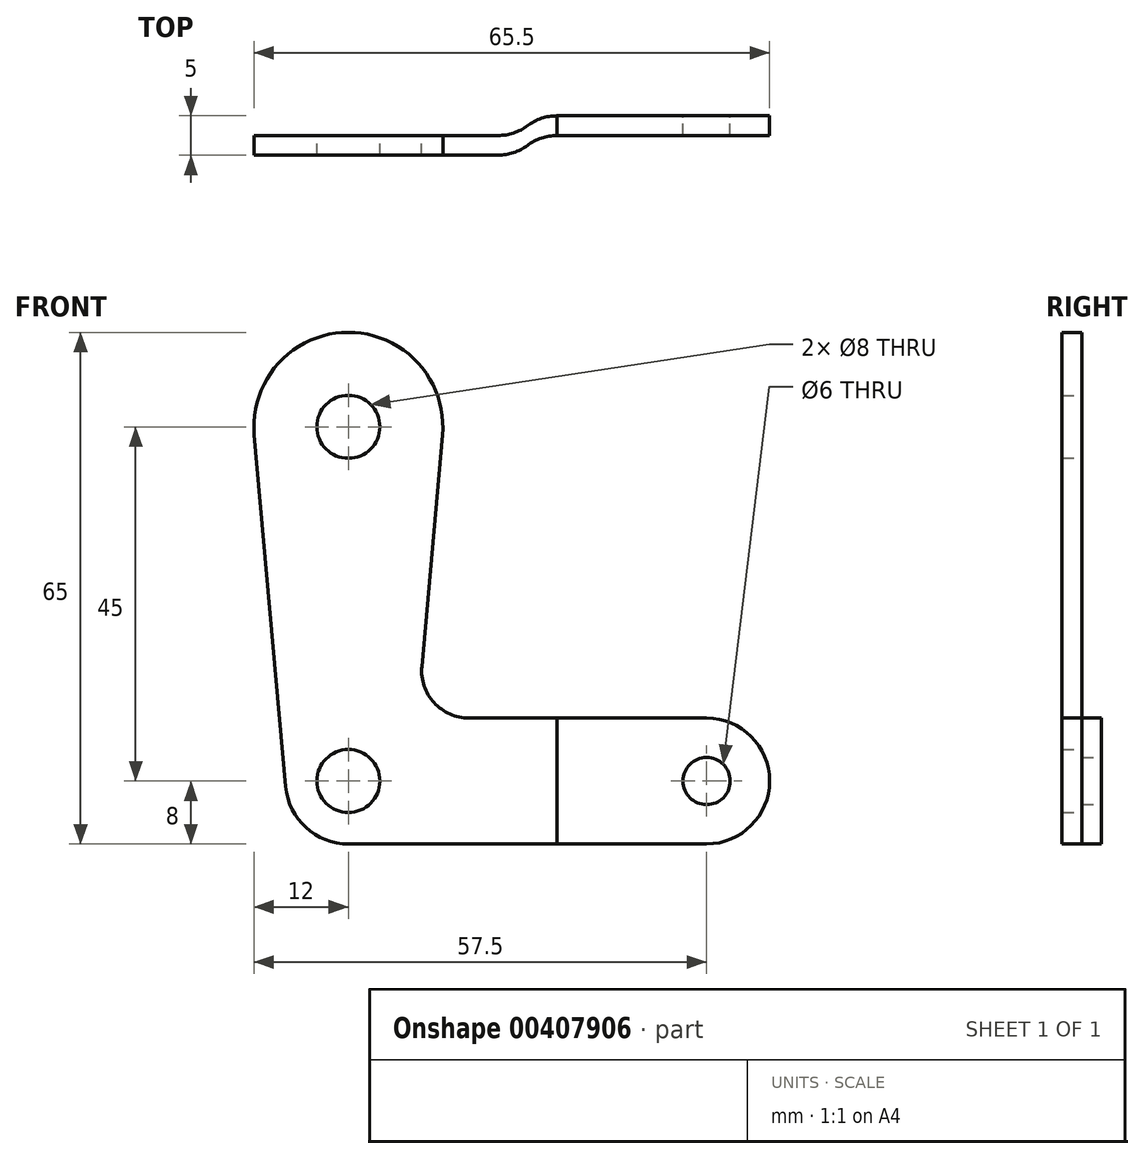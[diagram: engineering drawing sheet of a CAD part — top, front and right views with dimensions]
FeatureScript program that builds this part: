
annotation { "Feature Type Name" : "Feature", "Feature Type Description" : "" }
export const myFeature = defineFeature(function(context is Context, id is Id, definition is map)
    precondition{}
    {
        {
            var Q0;
            Q0=qCreatedBy(makeId("Front.planeOp"),FACE);
            var sketch = newSketch(context, id + "F0", { "sketchPlane" : qUnion([Q0])});
            skCircle(sketch, "E0", {"center": v(0, 0) * mm, "radius": 4 * mm});
            skCircle(sketch, "E1", {"center": v(0, 45) * mm, "radius": 4 * mm});
            skArc(sketch, "E2", {"start": v(0, -8) * mm, "mid": v(-5.4, -5.9) * mm, "end": v(-7.97, -0.71) * mm});
            skArc(sketch, "E3", {"start": v(11.95, 43.93) * mm, "mid": v(0, 57) * mm, "end": v(-11.95, 43.93) * mm});
            skLineSegment(sketch, "E4", {"start": v(-11.95, 43.93) * mm, "end": v(-7.97, -0.71) * mm});
            skLineSegment(sketch, "E5", {"start": v(11.95, 43.93) * mm, "end": v(9.33, 14.53) * mm});
            skArc(sketch, "E6", {"start": v(9.33, 14.53) * mm, "mid": v(10.88, 9.95) * mm, "end": v(15.3, 8) * mm});
            skLineSegment(sketch, "E7", {"start": v(15.3, 8) * mm, "end": v(19, 8) * mm});
            skLineSegment(sketch, "E8", {"start": v(0, -8) * mm, "end": v(19, -8) * mm});
            skLineSegment(sketch, "E9", {"start": v(19, 8) * mm, "end": v(19, -8) * mm});
            skSolve(sketch);
        }
        {
            var Q0;
            Q0=makeQuery(id+"F0.imprint","IMPRINT",FACE,{"disambiguationData":[TD([[makeQuery(id+"F0.imprint","IMPRINT",EDGE,{"derivedFrom":sQuery(id+"F0.wireOp",EDGE,"E0")}),-1.0]])]});
            extrude(context, id + "F1", {"entities" : qUnion([Q0]), "depth" : 2.5 * mm});
        }
        {
            var Q0;
            Q0=qCreatedBy(makeId("Top.planeOp"),FACE);
            var sketch = newSketch(context, id + "F2", { "sketchPlane" : qUnion([Q0])});
            skPoint(sketch, "E10.0", {"position": v(19, -2.5) * mm});
            skPoint(sketch, "E11.0", {"position": v(19, 0) * mm});
            skLineSegment(sketch, "E12.0", {"start": v(19, -2.5) * mm, "end": v(19, 0) * mm});
            skLineSegment(sketch, "E13", {"start": v(26.5, 2.5) * mm, "end": v(26.5, 0) * mm});
            skArc(sketch, "E14", {"start": v(19, -2.5) * mm, "mid": v(20.98, -2.18) * mm, "end": v(22.75, -1.25) * mm});
            skArc(sketch, "E15", {"start": v(26.5, 0) * mm, "mid": v(24.52, -0.32) * mm, "end": v(22.75, -1.25) * mm});
            skArc(sketch, "E16", {"start": v(19, 0) * mm, "mid": v(20.98, 0.32) * mm, "end": v(22.75, 1.25) * mm});
            skArc(sketch, "E17", {"start": v(26.5, 2.5) * mm, "mid": v(24.52, 2.18) * mm, "end": v(22.75, 1.25) * mm});
            skSolve(sketch);
        }
        {
            var Q0;
            Q0=makeQuery(id+"F2.imprint","IMPRINT",FACE,{"disambiguationData":[TD([[makeQuery(id+"F2.imprint","IMPRINT",EDGE,{"derivedFrom":sQuery(id+"F2.wireOp",EDGE,"E12.0")}),-1.0]])]});
            extrude(context, id + "F3", {"entities" : qUnion([Q0]), "operationType" : NewBodyOperationType.ADD, "endBound" : BoundingType.SYMMETRIC, "depth" : 16 * mm});
        }
        {
            var Q0;
            Q0=makeQuery(id+"F1.opExtrude","CAP_FACE",FACE,{"disambiguationData":[OSD([sQuery(id+"F0.wireOp",EDGE,"E0"),sQuery(id+"F0.wireOp",EDGE,"E1"),sQuery(id+"F0.wireOp",EDGE,"E2"),sQuery(id+"F0.wireOp",EDGE,"E3"),sQuery(id+"F0.wireOp",EDGE,"E4"),sQuery(id+"F0.wireOp",EDGE,"E5"),sQuery(id+"F0.wireOp",EDGE,"E6"),sQuery(id+"F0.wireOp",EDGE,"E7"),sQuery(id+"F0.wireOp",EDGE,"E8"),sQuery(id+"F0.wireOp",EDGE,"E9")])],"isStart":false});
            cPlane(context, id + "F4", {"entities" : qUnion([Q0]), "cplaneType" : CPlaneType.OFFSET, "offset" : 5 * mm, "oppositeDirection" : true, "width" : 150 * mm, "height" : 150 * mm});
        }
        {
            var Q0;
            Q0=qCreatedBy(id+"F4.planeOp",FACE);
            var sketch = newSketch(context, id + "F5", { "sketchPlane" : qUnion([Q0])});
            skPoint(sketch, "E18.0", {"position": v(26.5, 8) * mm});
            skPoint(sketch, "E19.0", {"position": v(26.5, -8) * mm});
            skLineSegment(sketch, "E20.0", {"start": v(26.5, -8) * mm, "end": v(26.5, 8) * mm});
            skLineSegment(sketch, "E21", {"start": v(26.5, -8) * mm, "end": v(45.5, -8) * mm});
            skLineSegment(sketch, "E22", {"start": v(26.5, 8) * mm, "end": v(45.5, 8) * mm});
            skArc(sketch, "E23", {"start": v(45.5, -8) * mm, "mid": v(53.5, 0) * mm, "end": v(45.5, 8) * mm});
            skCircle(sketch, "E24", {"center": v(45.5, 0) * mm, "radius": 3 * mm});
            skSolve(sketch);
        }
        {
            var Q0;
            Q0=makeQuery(id+"F5.imprint","IMPRINT",FACE,{"disambiguationData":[TD([[makeQuery(id+"F5.imprint","IMPRINT",EDGE,{"derivedFrom":sQuery(id+"F5.wireOp",EDGE,"E20.0")}),1.0]])]});
            var Q1;
            Q1=makeQuery(id+"F5.imprint","IMPRINT",FACE,{"disambiguationData":[TD([[makeQuery(id+"F5.imprint","IMPRINT",EDGE,{"derivedFrom":sQuery(id+"F5.wireOp",EDGE,"E20.0")}),-1.0]])]});
            extrude(context, id + "F6", {"entities" : qUnion([Q0, Q1]), "depth" : 2.5 * mm});
        }
    });
